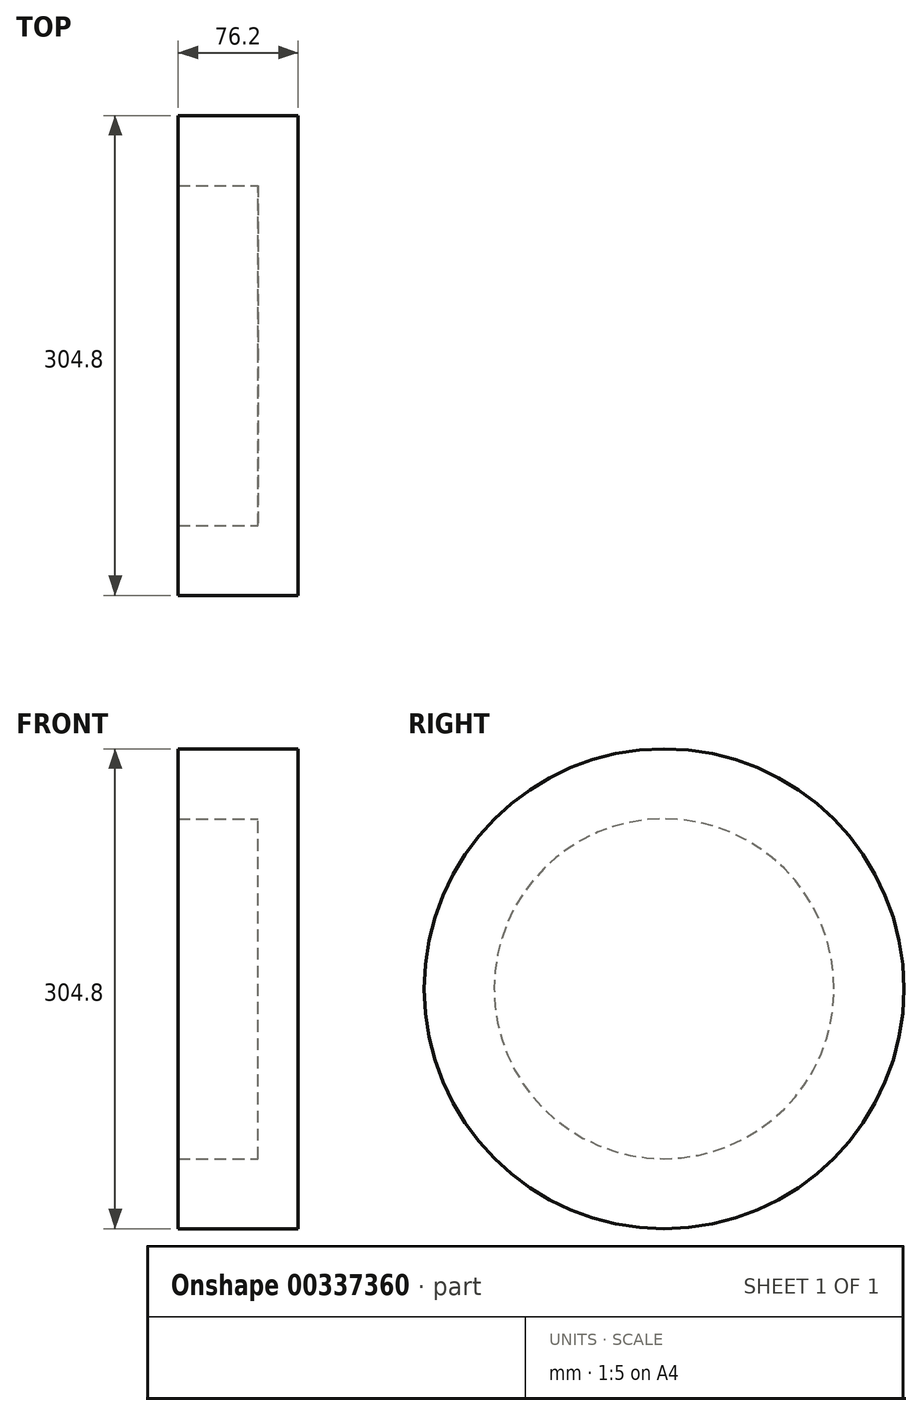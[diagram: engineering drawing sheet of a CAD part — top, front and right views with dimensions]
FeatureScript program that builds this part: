
annotation { "Feature Type Name" : "Feature", "Feature Type Description" : "" }
export const myFeature = defineFeature(function(context is Context, id is Id, definition is map)
    precondition{}
    {
        {
            var Q0;
            Q0=qCreatedBy(makeId("Right.planeOp"),FACE);
            var sketch = newSketch(context, id + "F0", { "sketchPlane" : qUnion([Q0])});
            skCircle(sketch, "E0", {"center": v(-39.1, -9.02) * mm, "radius": 152.4 * mm});
            skCircle(sketch, "E1", {"center": v(-39.1, -9.02) * mm, "radius": 107.95 * mm});
            skSolve(sketch);
        }
        {
            var Q0;
            Q0 = qSketchRegion(id + "F0", true);
            extrude(context, id + "F1", {"entities" : qUnion([Q0]), "oppositeDirection" : true, "depth" : 76.2 * mm});
        }
        {
            var Q0;
            Q0=makeQuery(id+"F0.imprint","IMPRINT",FACE,{"disambiguationData":[TD([[makeQuery(id+"F0.imprint","IMPRINT",EDGE,{"derivedFrom":sQuery(id+"F0.wireOp",EDGE,"E1")}),1.0]])]});
            extrude(context, id + "F2", {"entities" : qUnion([Q0]), "operationType" : NewBodyOperationType.ADD, "oppositeDirection" : true, "depth" : 25.4 * mm});
        }
    });
